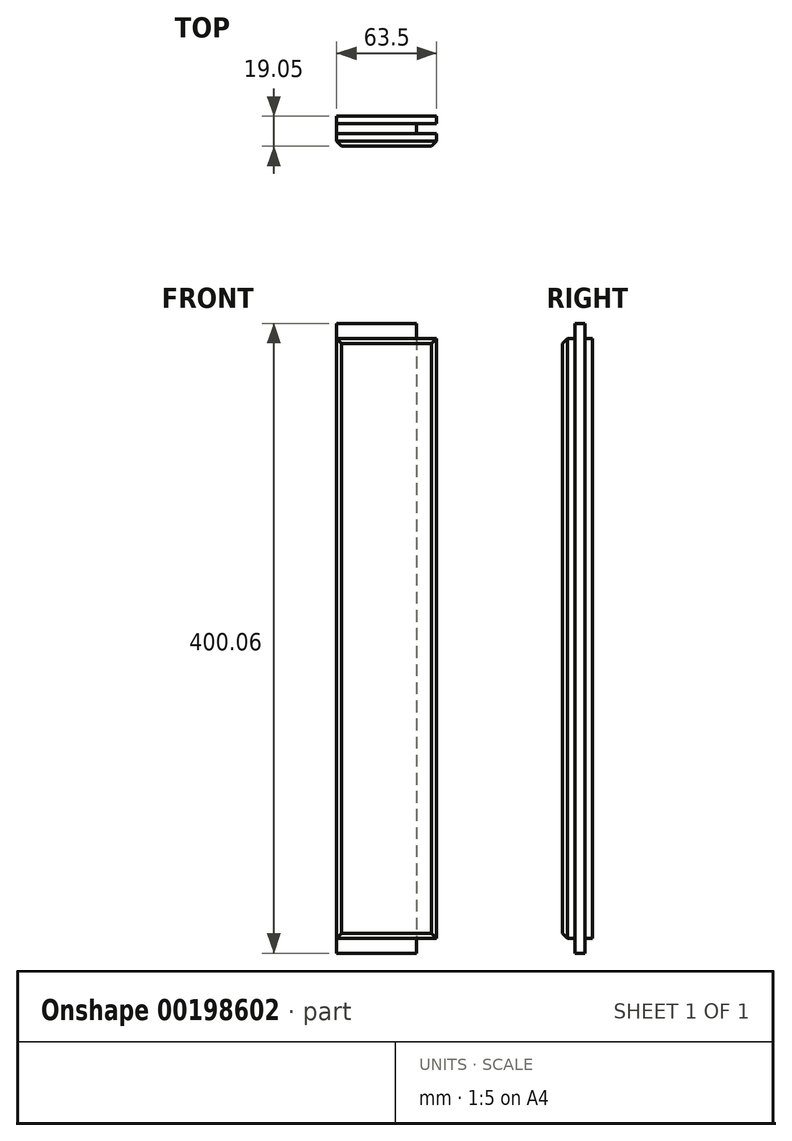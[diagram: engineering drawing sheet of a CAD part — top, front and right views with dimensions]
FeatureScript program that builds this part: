
annotation { "Feature Type Name" : "Feature", "Feature Type Description" : "" }
export const myFeature = defineFeature(function(context is Context, id is Id, definition is map)
    precondition{}
    {
        {
            var Q0;
            Q0=qCreatedBy(makeId("Top.planeOp"),FACE);
            var sketch = newSketch(context, id + "F0", { "sketchPlane" : qUnion([Q0])});
            skLineSegment(sketch, "E0.bottom", {"start": v(0, 0) * mm, "end": v(63.5, 0) * mm});
            skLineSegment(sketch, "E0.top", {"start": v(0, 19.05) * mm, "end": v(63.5, 19.05) * mm});
            skLineSegment(sketch, "E0.left", {"start": v(0, 0) * mm, "end": v(0, 19.05) * mm});
            skLineSegment(sketch, "E0.right", {"start": v(63.5, 0) * mm, "end": v(63.5, 19.05) * mm});
            skSolve(sketch);
        }
        {
            var Q0;
            Q0=makeQuery(id+"F0.imprint","IMPRINT",FACE,{"disambiguationData":[TD([[makeQuery(id+"F0.imprint","IMPRINT",EDGE,{"derivedFrom":sQuery(id+"F0.wireOp",EDGE,"E0.bottom")}),1.0]])]});
            extrude(context, id + "F1", {"entities" : qUnion([Q0]), "depth" : 381 * mm});
        }
        {
            var Q0;
            Q0=makeQuery(id+"F1.opExtrude","SWEPT_EDGE",EDGE,{"disambiguationData":[OSD([sQuery(id+"F0.wireOp",EDGE,"E0.bottom"),sQuery(id+"F0.wireOp",EDGE,"E0.left")])]});
            var Q1;
            Q1=makeQuery(id+"F1.opExtrude","SWEPT_EDGE",EDGE,{"disambiguationData":[OSD([sQuery(id+"F0.wireOp",EDGE,"E0.bottom"),sQuery(id+"F0.wireOp",EDGE,"E0.right")])]});
            var Q2;
            Q2=makeQuery(id+"F1.opExtrude","CAP_EDGE",EDGE,{"disambiguationData":[OSD([sQuery(id+"F0.wireOp",EDGE,"E0.bottom")])],"isStart":false});
            var Q3;
            Q3=makeQuery(id+"F1.opExtrude","CAP_EDGE",EDGE,{"disambiguationData":[OSD([sQuery(id+"F0.wireOp",EDGE,"E0.bottom")])],"isStart":true});
            chamfer(context, id + "F2", {"entities" : qUnion([Q0, Q1, Q2, Q3]), "width" : 3.17 * mm, "tangentPropagation" : true});
        }
        {
            var Q0;
            Q0=makeQuery(id+"F1.opExtrude","CAP_FACE",FACE,{"disambiguationData":[OSD([sQuery(id+"F0.wireOp",EDGE,"E0.bottom"),sQuery(id+"F0.wireOp",EDGE,"E0.top"),sQuery(id+"F0.wireOp",EDGE,"E0.left"),sQuery(id+"F0.wireOp",EDGE,"E0.right")])],"isStart":true});
            var sketch = newSketch(context, id + "F3", { "sketchPlane" : qUnion([Q0])});
            skLineSegment(sketch, "E1", {"start": v(63.5, -14.29) * mm, "end": v(50.8, -14.29) * mm});
            skLineSegment(sketch, "E2", {"start": v(50.8, -14.29) * mm, "end": v(50.8, -7.94) * mm});
            skLineSegment(sketch, "E3", {"start": v(50.8, -7.94) * mm, "end": v(63.5, -7.94) * mm});
            skLineSegment(sketch, "E4", {"start": v(63.5, -7.94) * mm, "end": v(63.5, -14.29) * mm});
            skSolve(sketch);
        }
        {
            var Q0;
            Q0 = qSketchRegion(id + "F3", true);
            extrude(context, id + "F4", {"entities" : qUnion([Q0]), "operationType" : NewBodyOperationType.REMOVE, "endBound" : BoundingType.THROUGH_ALL, "oppositeDirection" : true, "depth" : 25.4 * mm});
        }
        {
            var Q0;
            Q0=makeQuery(id+"F1.opExtrude","SWEPT_FACE",FACE,{"disambiguationData":[OSD([sQuery(id+"F0.wireOp",EDGE,"E0.left")])]});
            var sketch = newSketch(context, id + "F5", { "sketchPlane" : qUnion([Q0])});
            skLineSegment(sketch, "E5", {"start": v(-14.29, 381) * mm, "end": v(-14.29, 390.53) * mm});
            skLineSegment(sketch, "E6", {"start": v(-14.29, 390.53) * mm, "end": v(-7.94, 390.53) * mm});
            skLineSegment(sketch, "E7", {"start": v(-7.94, 390.53) * mm, "end": v(-7.94, 381) * mm});
            skLineSegment(sketch, "E8", {"start": v(-7.94, 381) * mm, "end": v(-14.29, 381) * mm});
            skLineSegment(sketch, "E9", {"start": v(-14.29, 0) * mm, "end": v(-14.29, -9.53) * mm});
            skLineSegment(sketch, "E10", {"start": v(-14.29, -9.53) * mm, "end": v(-7.94, -9.53) * mm});
            skLineSegment(sketch, "E11", {"start": v(-7.94, -9.53) * mm, "end": v(-7.94, 0) * mm});
            skLineSegment(sketch, "E12", {"start": v(-7.94, 0) * mm, "end": v(-14.29, 0) * mm});
            skSolve(sketch);
        }
        {
            var Q0;
            Q0 = qSketchRegion(id + "F5", true);
            extrude(context, id + "F6", {"entities" : qUnion([Q0]), "operationType" : NewBodyOperationType.ADD, "oppositeDirection" : true, "depth" : 50.8 * mm});
        }
    });
